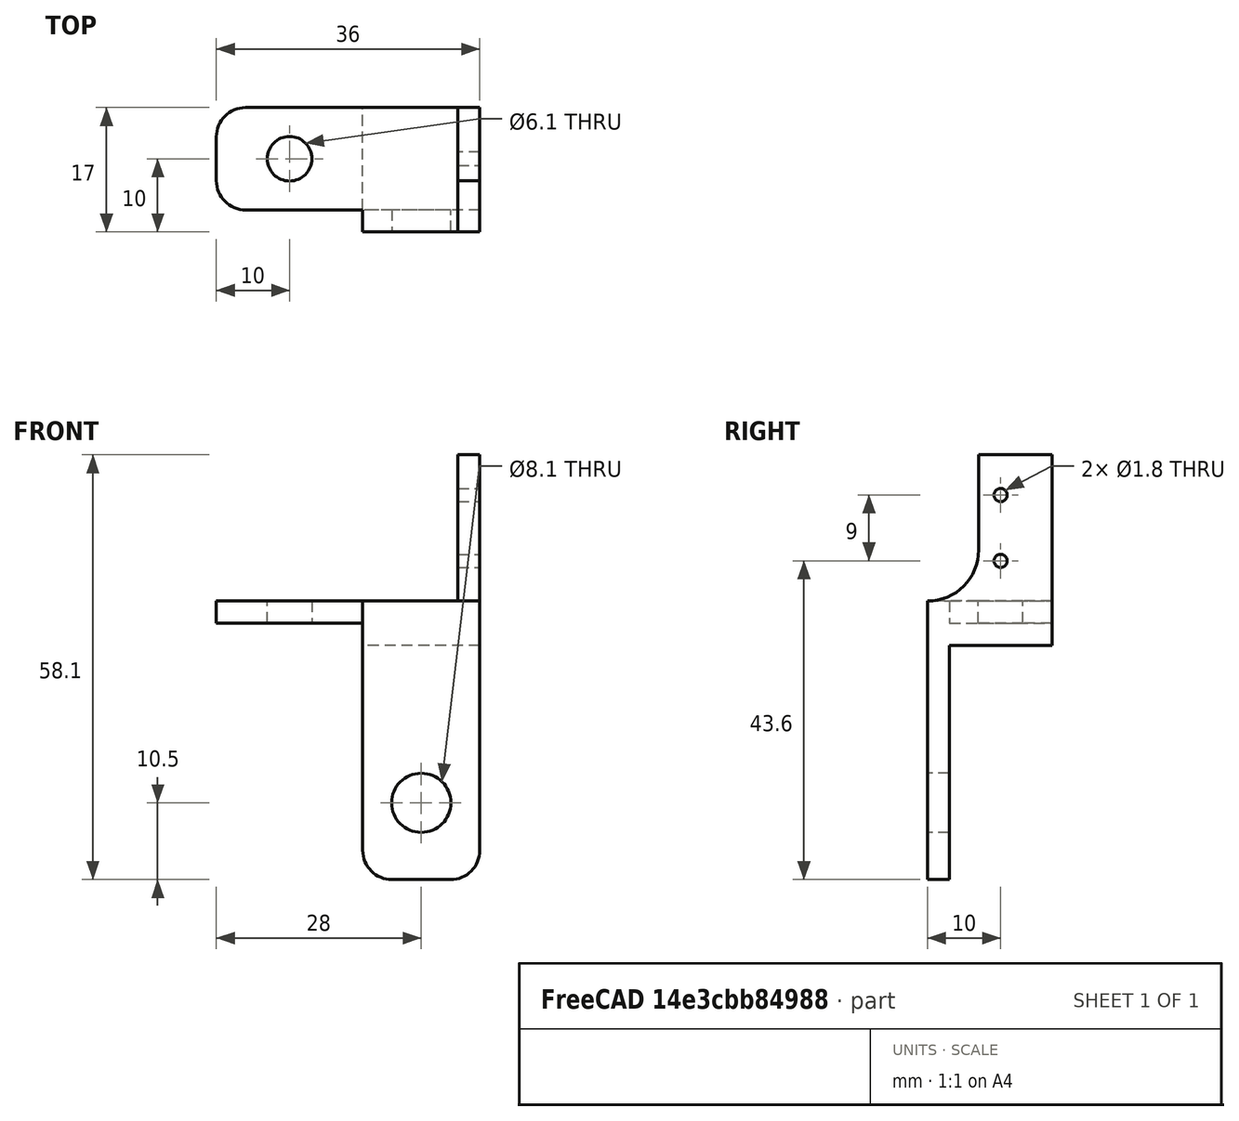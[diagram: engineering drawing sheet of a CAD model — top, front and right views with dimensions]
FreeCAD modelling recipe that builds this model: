
FCSTD DOCUMENT  (FreeCAD 0.21R33771 (Git))
Label: x_end_stop
License: All rights reserved
LicenseURL: https://en.wikipedia.org/wiki/All_rights_reserved
objects: Sketcher::SketchObject×7, PartDesign::Pad×4, PartDesign::Pocket×3, PartDesign::Fillet×2, PartDesign::Body×1, Mesh::Feature×1
note: 26 computed .brp shape members not serialized (recipe doc carries the construction recipe); baked Part::Feature solids carry a one-line shape summary decoded from their .brp

FEATURE [Sketcher::SketchObject] Sketch
  FullyConstrained = true
  MapMode = 5
  Support = -> [XY_Plane]
  sketch-geometry (4):
    g0: LineSegment StartX=-8 StartY=8.5 StartZ=0 EndX=8 EndY=8.5 EndZ=0
    g1: LineSegment StartX=8 StartY=8.5 StartZ=0 EndX=8 EndY=-8.5 EndZ=0
    g2: LineSegment StartX=8 StartY=-8.5 StartZ=0 EndX=-8 EndY=-8.5 EndZ=0
    g3: LineSegment StartX=-8 StartY=-8.5 StartZ=0 EndX=-8 EndY=8.5 EndZ=0
  constraints (10):
    c: Coincident(g0,g1)
    c: Coincident(g1,g2)
    c: Coincident(g2,g3)
    c: Coincident(g3,g0)
    c: Horizontal(g2)
    c: Vertical(g1)
    c: DistanceY(g1,g1) = 17
    c: DistanceX(g0,g0) = 16
    c: Symmetric(g0,g2,g-1)
    c: Symmetric(g0,g0,g-2)
FEATURE [PartDesign::Pad] Pad
  Direction = (0,0,1)
  Length = 6.1
  Length2 = 10
  Profile = -> Sketch
  ReferenceAxis = -> Sketch [N_Axis]
  Type = 0
FEATURE [Sketcher::SketchObject] Sketch001
  ExternalGeometry = -> [Pad]
  FullyConstrained = true
  MapMode = 5
  Placement = pos=(0,0,0) rot=(1,0,0;3.14159rad)
  Support = -> [Pad]
  sketch-geometry (4):
    g0: LineSegment StartX=-8 StartY=8.5 StartZ=0 EndX=8 EndY=8.5 EndZ=0
    g1: LineSegment StartX=8 StartY=8.5 StartZ=0 EndX=8 EndY=5.5 EndZ=0
    g2: LineSegment StartX=8 StartY=5.5 StartZ=0 EndX=-8 EndY=5.5 EndZ=0
    g3: LineSegment StartX=-8 StartY=5.5 StartZ=0 EndX=-8 EndY=8.5 EndZ=0
  constraints (10):
    c: Coincident(g0,g1)
    c: Coincident(g1,g2)
    c: Coincident(g2,g3)
    c: Coincident(g3,g0)
    c: Horizontal(g2)
    c: Vertical(g1)
    c: Vertical(g3)
    c: DistanceY(g1,g1) = 3
    c: Coincident(g0,g-3)
    c: Coincident(g0,g-3)
FEATURE [PartDesign::Pad] Pad001
  BaseFeature = -> Pad
  Direction = (0,0,-1)
  Length = 32
  Length2 = 10
  Profile = -> Sketch001
  ReferenceAxis = -> Sketch001 [N_Axis]
  Type = 0
FEATURE [Sketcher::SketchObject] Sketch002
  ExternalGeometry = -> [Pad001]
  FullyConstrained = true
  MapMode = 5
  Placement = pos=(0,-8.5,0) rot=(1,0,0;1.5708rad)
  Support = -> [Pad001]
  sketch-geometry (1):
    g0: Circle CenterX=0 CenterY=-21.5 CenterZ=0 NormalX=0 NormalY=0 NormalZ=1 AngleXU=0 Radius=4.05
  constraints (3):
    c: PointOnObject(g0,g-2)
    c: Diameter(g0) = 8.1
    c: DistanceY(g0,g-3) = 21.5
FEATURE [PartDesign::Pocket] Pocket
  BaseFeature = -> Pad001
  Direction = (0,1,-2e-16)
  Length = 5
  Length2 = 5
  Profile = -> Sketch002
  ReferenceAxis = -> Sketch002 [N_Axis]
  Type = 1
FEATURE [Sketcher::SketchObject] Sketch003
  ExternalGeometry = -> [Pocket]
  FullyConstrained = true
  MapMode = 5
  Placement = pos=(-8,0,0) rot=(0.57735,-0.57735,-0.57735;2.0944rad)
  Support = -> [Pocket]
  sketch-geometry (4):
    g0: LineSegment StartX=-8.5 StartY=6.1 StartZ=0 EndX=5.5 EndY=6.1 EndZ=0
    g1: LineSegment StartX=5.5 StartY=6.1 StartZ=0 EndX=5.5 EndY=3.1 EndZ=0
    g2: LineSegment StartX=5.5 StartY=3.1 StartZ=0 EndX=-8.5 EndY=3.1 EndZ=0
    g3: LineSegment StartX=-8.5 StartY=3.1 StartZ=0 EndX=-8.5 EndY=6.1 EndZ=0
  constraints (11):
    c: Coincident(g0,g1)
    c: Coincident(g1,g2)
    c: Coincident(g2,g3)
    c: Coincident(g3,g0)
    c: Horizontal(g2)
    c: Vertical(g1)
    c: Vertical(g3)
    c: DistanceY(g1,g1) = 3
    c: Coincident(g0,g-3)
    c: DistanceX(g0,g-3) = 3
    c: Horizontal(g0)
FEATURE [PartDesign::Pad] Pad002
  BaseFeature = -> Pocket
  Direction = (-1,0,0)
  Length = 20
  Length2 = 10
  Profile = -> Sketch003
  ReferenceAxis = -> Sketch003 [N_Axis]
  Type = 0
FEATURE [Sketcher::SketchObject] Sketch005
  FullyConstrained = false
  MapMode = 5
  Placement = pos=(0,0,6.1) rot=(0,0,1;0rad)
  sketch-geometry (4):
    g0: LineSegment StartX=5 StartY=8.5 StartZ=0 EndX=8 EndY=8.5 EndZ=0
    g1: LineSegment StartX=8 StartY=8.5 StartZ=0 EndX=8 EndY=-1.5 EndZ=0
    g2: LineSegment StartX=8 StartY=-1.5 StartZ=0 EndX=5 EndY=-1.5 EndZ=0
    g3: LineSegment StartX=5 StartY=-1.5 StartZ=0 EndX=5 EndY=8.5 EndZ=0
  constraints (10):
    c: Coincident(g0,g1)
    c: Coincident(g1,g2)
    c: Coincident(g2,g3)
    c: Coincident(g3,g0)
    c: Horizontal(g0)
    c: Horizontal(g2)
    c: Vertical(g3)
    c: DistanceX(g0,g0) = 3
    c: DistanceY(g3,g3) = 10
    c: Vertical(g1,g0)
FEATURE [PartDesign::Pad] Pad003
  BaseFeature = -> Pad002
  Direction = (0,0,1)
  Length = 20
  Length2 = 10
  Profile = -> Sketch005
  ReferenceAxis = -> Sketch005 [N_Axis]
  Type = 0
FEATURE [Sketcher::SketchObject] Sketch006
  ExternalGeometry = -> [Pad003]
  FullyConstrained = true
  MapMode = 5
  Placement = pos=(0,0,6.1) rot=(0,0,1;0rad)
  Support = -> [Pad003]
  sketch-geometry (2):
    g0: Circle CenterX=-18 CenterY=1.5 CenterZ=0 NormalX=0 NormalY=0 NormalZ=1 AngleXU=0 Radius=3.05
    g1: LineSegment StartX=-28 StartY=1.5 StartZ=0 EndX=0 EndY=1.5 EndZ=0
  constraints (6):
    c: Diameter(g0) = 6.1
    c: PointOnObject(g1,g-3)
    c: PointOnObject(g1,g-2)
    c: Symmetric(g-3,g-3,g1)
    c: PointOnObject(g0,g1)
    c: DistanceX(g-3,g0) = 10
FEATURE [PartDesign::Pocket] Pocket001
  BaseFeature = -> Pad003
  Direction = (0,0,-1)
  Length = 5
  Length2 = 5
  Profile = -> Sketch006
  ReferenceAxis = -> Sketch006 [N_Axis]
  Type = 1
FEATURE [Sketcher::SketchObject] Sketch007
  ExternalGeometry = -> [Pocket001]
  FullyConstrained = true
  MapMode = 5
  Placement = pos=(8,0,0) rot=(0.57735,0.57735,0.57735;2.0944rad)
  Support = -> [Pocket001]
  sketch-geometry (2):
    g0: Circle CenterX=1.5 CenterY=20.6 CenterZ=0 NormalX=0 NormalY=0 NormalZ=1 AngleXU=0 Radius=0.9
    g1: Circle CenterX=1.5 CenterY=11.6 CenterZ=0 NormalX=0 NormalY=0 NormalZ=1 AngleXU=0 Radius=0.9
  constraints (6):
    c: Equal(g1,g0)
    c: Vertical(g1,g0)
    c: Diameter(g1) = 1.8
    c: DistanceY(g1,g0) = 9
    c: DistanceX(g0,g-3) = 7
    c: DistanceY(g0,g-3) = 5.5
FEATURE [PartDesign::Pocket] Pocket002
  BaseFeature = -> Pocket001
  Direction = (-1,0,0)
  Length = 5
  Length2 = 5
  Profile = -> Sketch007
  ReferenceAxis = -> Sketch007 [N_Axis]
  Type = 1
FEATURE [PartDesign::Fillet] Fillet
  Base = -> Pocket002 [Edge23]
  BaseFeature = -> Pocket002
  Radius = 6.99
  SupportTransform = false
  UseAllEdges = false
FEATURE [PartDesign::Fillet] Fillet001
  Base = -> Fillet [Edge25,Edge56,Edge62,Edge58]
  BaseFeature = -> Fillet
  Radius = 4
  SupportTransform = false
  UseAllEdges = false
FEATURE [PartDesign::Body] Body
  Group = -> [Sketch,Pad,Sketch001,Pad001,Sketch002,Pocket,Sketch003,Pad002,Sketch005,Pad003,Sketch006,Pocket001,Sketch007,Pocket002,Fillet,Fillet001]
  Origin = -> Origin
  Tip = -> Fillet001
FEATURE [Mesh::Feature] Mesh  label="Fillet001 (Meshed)"
